# Revit family: 1105001 Nena
name_source: partatom
category: Lighting Fixtures
revit_build: Autodesk Revit 2018 (Build: 20170223_1515(x64)
units: mm (PartAtom-declared; Revit-internal decimal feet)

## family parameters
Always vertical = Yes
Cut with Voids When Loaded = No
Host = Wall
Light Source = No
OmniClass Number = 23.80.70.00
OmniClass Title = Lighting
Part Type = Normal
Room Calculation Point = No
Round Connector Dimension = Use Diameter
Shared = No

## types (2) — shared parameters
Driver Required = No
Manufacturer = Astro Lighting Ltd
Manufacturer URL - Europe and Rest of World = www.astrolighting.com
Manufacturer URL - North America = us.astrolighting.com
Product Location = Bathroom
URL = www.astrolighting.com

## per-type parameters (varying)
| type | ADA compliant | Dimmable | Dimming Method | Driver Included | Efficacy (lm/w) | Electrical Class | Lamp | Length of Cable Supplied | Light Source Fixed | Location / IP Rating | Main Finish | Main Material | Power (Watts) | Product CCT | Product CRI | Product Dimensions (MM) | Product Name | Product SKU | Product URL | Product Weight (KG) | Wattage Comments |
| CE | Not Applicable | Yes | Lamp Dependant | Not Applicable | Lamp Dependant | 2 | 1 x 3W Max LED G9 | Not Applicable | Yes | IP44 | Polished Chrome | Metal - Mild Steel | 1 x 25W Max G9 | Lamp Dependant | Lamp Dependant | 160 x 140 x 190 | Nena | 1105001 | https://www.astrolighting.com | 0.76 | Not Applicable |
| ETL |  |  |  |  |  | 0 |  |  |  | DAMP |  | Metal - Steel |  | 2700K / 3000K | 80 / 90 |  |  | 1234001 |  |  |  |

## geometry (parser evidence)
native form markers: Sweep x2
no freeform markers — native parametric forms only
